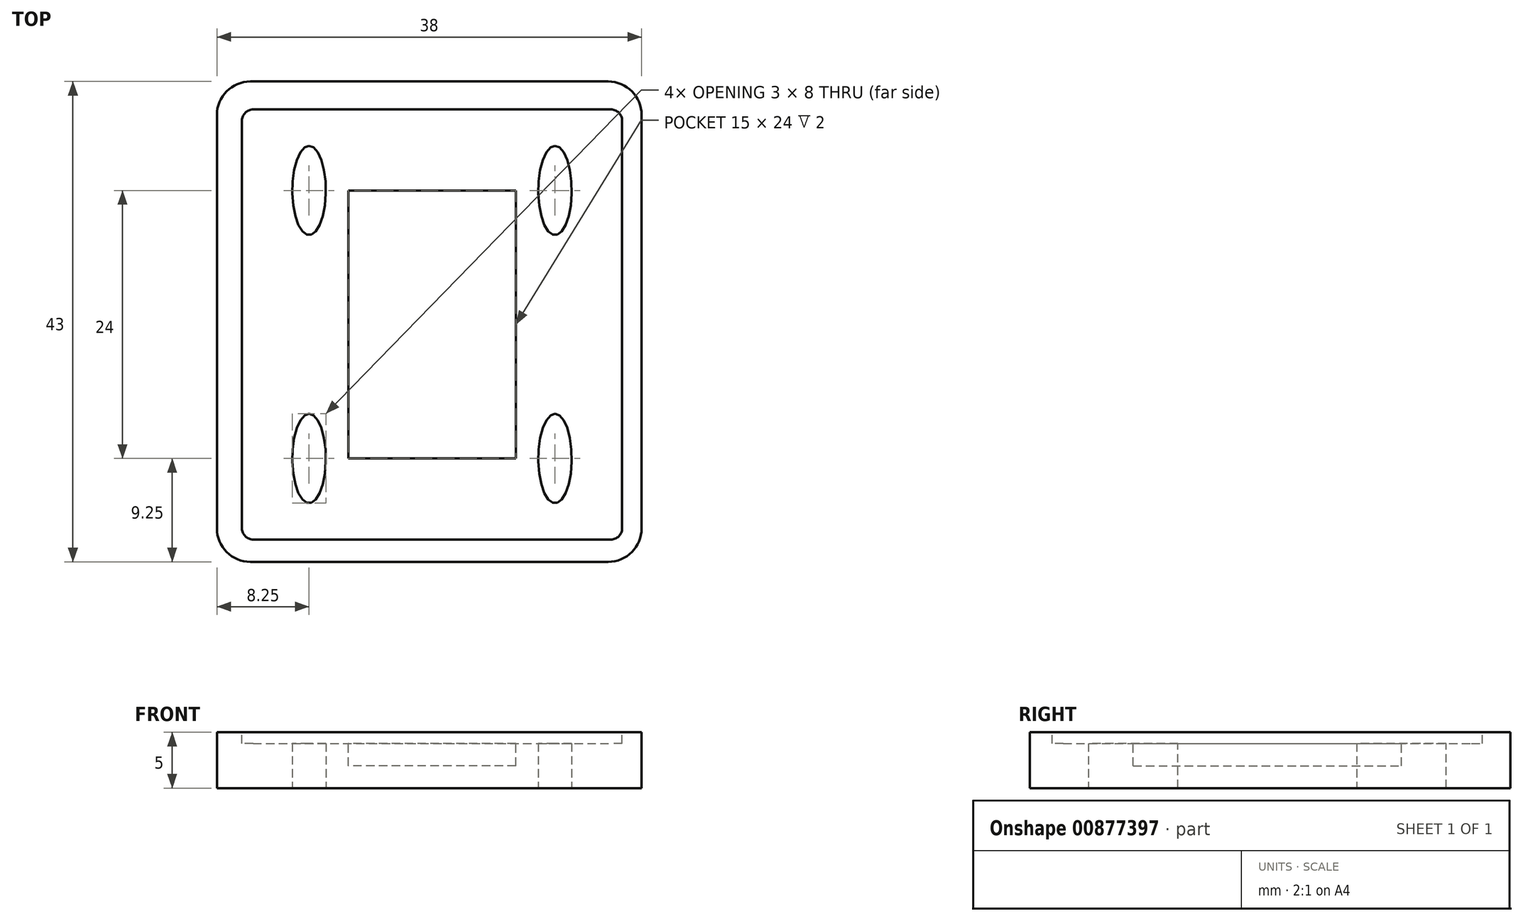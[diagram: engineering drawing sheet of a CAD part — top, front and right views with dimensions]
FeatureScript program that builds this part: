
annotation { "Feature Type Name" : "Feature", "Feature Type Description" : "" }
export const myFeature = defineFeature(function(context is Context, id is Id, definition is map)
    precondition{}
    {
        {
            var Q0;
            Q0=qCreatedBy(makeId("Top.planeOp"),FACE);
            var sketch = newSketch(context, id + "F0", { "sketchPlane" : qUnion([Q0])});
            skLineSegment(sketch, "E0.bottom", {"start": v(0, 0) * mm, "end": v(38, 0) * mm});
            skLineSegment(sketch, "E0.top", {"start": v(0, 43) * mm, "end": v(38, 43) * mm});
            skLineSegment(sketch, "E0.left", {"start": v(0, 0) * mm, "end": v(0, 43) * mm});
            skLineSegment(sketch, "E0.right", {"start": v(38, 0) * mm, "end": v(38, 43) * mm});
            skSolve(sketch);
        }
        {
            var Q0;
            Q0 = qSketchRegion(id + "F0", true);
            var Q1;
            Q1=makeQuery(id+"F0.imprint","IMPRINT",FACE,{"disambiguationData":[TD([[makeQuery(id+"F0.imprint","IMPRINT",EDGE,{"derivedFrom":sQuery(id+"F0.wireOp",EDGE,"M4hEIno1-cevh-JGJ9-cI0y-gHAv0wphkMzr")}),1.0]])]});
            extrude(context, id + "F1", {"entities" : qUnion([Q0, Q1]), "depth" : 5 * mm, "offsetDistance" : 25 * mm});
        }
        {
            var Q0;
            Q0=makeQuery(id+"F1.opExtrude","CAP_FACE",FACE,{"disambiguationData":[OSD([sQuery(id+"F0.wireOp",EDGE,"E0.bottom"),sQuery(id+"F0.wireOp",EDGE,"E0.top"),sQuery(id+"F0.wireOp",EDGE,"E0.left"),sQuery(id+"F0.wireOp",EDGE,"E0.right")])],"isStart":false});
            var sketch = newSketch(context, id + "F2", { "sketchPlane" : qUnion([Q0])});
            skLineSegment(sketch, "E1.bottom", {"start": v(2.25, 2) * mm, "end": v(36.25, 2) * mm});
            skLineSegment(sketch, "E1.top", {"start": v(2.25, 40.5) * mm, "end": v(36.25, 40.5) * mm});
            skLineSegment(sketch, "E1.left", {"start": v(2.25, 2) * mm, "end": v(2.25, 40.5) * mm});
            skLineSegment(sketch, "E1.right", {"start": v(36.25, 2) * mm, "end": v(36.25, 40.5) * mm});
            skSolve(sketch);
        }
        {
            var Q0;
            Q0=makeQuery(id+"F2.imprint","IMPRINT",FACE,{"disambiguationData":[TD([[makeQuery(id+"F2.imprint","IMPRINT",EDGE,{"derivedFrom":sQuery(id+"F2.wireOp",EDGE,"E1.bottom")}),1.0]])]});
            extrude(context, id + "F3", {"entities" : qUnion([Q0]), "operationType" : NewBodyOperationType.REMOVE, "oppositeDirection" : true, "depth" : 1 * mm, "offsetDistance" : 25 * mm});
        }
        {
            var Q0;
            Q0=makeQuery(id+"F3.boolean.opBoolean","COPY",FACE,{"derivedFrom":makeQuery(id+"F3.opExtrude","CAP_FACE",FACE,{"disambiguationData":[OSD([sQuery(id+"F2.wireOp",EDGE,"E1.bottom"),sQuery(id+"F2.wireOp",EDGE,"E1.top"),sQuery(id+"F2.wireOp",EDGE,"E1.left"),sQuery(id+"F2.wireOp",EDGE,"E1.right")])],"isStart":false})});
            var sketch = newSketch(context, id + "F4", { "sketchPlane" : qUnion([Q0])});
            skEllipse(sketch, "E2", {"center": v(8.25, 9.25) * mm, "majorRadius": 4 * mm, "minorRadius": 1.5 * mm, "majorAxis": v(0, 1)});
            skEllipse(sketch, "E3.0.1.0", {"center": v(8.25, 33.25) * mm, "majorRadius": 4 * mm, "minorRadius": 1.5 * mm, "majorAxis": v(0, 1)});
            skEllipse(sketch, "E3.1.0.0", {"center": v(30.25, 9.25) * mm, "majorRadius": 4 * mm, "minorRadius": 1.5 * mm, "majorAxis": v(0, 1)});
            skEllipse(sketch, "E3.1.1.0", {"center": v(30.25, 33.25) * mm, "majorRadius": 4 * mm, "minorRadius": 1.5 * mm, "majorAxis": v(0, 1)});
            skLineSegment(sketch, "E3.direction2", {"start": v(8.25, 9.25) * mm, "end": v(8.25, 33.25) * mm, "construction": true});
            skLineSegment(sketch, "E4.bottom", {"start": v(26.75, 9.25) * mm, "end": v(11.75, 9.25) * mm});
            skLineSegment(sketch, "E4.top", {"start": v(26.75, 33.25) * mm, "end": v(11.75, 33.25) * mm});
            skLineSegment(sketch, "E4.left", {"start": v(26.75, 9.25) * mm, "end": v(26.75, 33.25) * mm});
            skLineSegment(sketch, "E4.right", {"start": v(11.75, 9.25) * mm, "end": v(11.75, 33.25) * mm});
            skSolve(sketch);
        }
        {
            var Q0;
            Q0=makeQuery(id+"F4.imprint","IMPRINT",FACE,{"disambiguationData":[TD([[makeQuery(id+"F4.imprint","IMPRINT",EDGE,{"derivedFrom":sQuery(id+"F4.wireOp",EDGE,"E3.0.1.0")}),1.0]])]});
            var Q1;
            Q1=makeQuery(id+"F4.imprint","IMPRINT",FACE,{"disambiguationData":[TD([[makeQuery(id+"F4.imprint","IMPRINT",EDGE,{"derivedFrom":sQuery(id+"F4.wireOp",EDGE,"E3.1.1.0")}),1.0]])]});
            var Q2;
            Q2=makeQuery(id+"F4.imprint","IMPRINT",FACE,{"disambiguationData":[TD([[makeQuery(id+"F4.imprint","IMPRINT",EDGE,{"derivedFrom":sQuery(id+"F4.wireOp",EDGE,"E3.1.0.0")}),1.0]])]});
            var Q3;
            Q3=makeQuery(id+"F4.imprint","IMPRINT",FACE,{"disambiguationData":[TD([[makeQuery(id+"F4.imprint","IMPRINT",EDGE,{"derivedFrom":sQuery(id+"F4.wireOp",EDGE,"E2")}),1.0]])]});
            extrude(context, id + "F5", {"entities" : qUnion([Q0, Q1, Q2, Q3]), "operationType" : NewBodyOperationType.REMOVE, "oppositeDirection" : true, "depth" : 25 * mm, "offsetDistance" : 25 * mm});
        }
        {
            var Q0;
            Q0=makeQuery(id+"F1.opExtrude","SWEPT_EDGE",EDGE,{"disambiguationData":[OSD([sQuery(id+"F0.wireOp",EDGE,"E0.bottom"),sQuery(id+"F0.wireOp",EDGE,"E0.left")])]});
            var Q1;
            Q1=makeQuery(id+"F1.opExtrude","SWEPT_EDGE",EDGE,{"disambiguationData":[OSD([sQuery(id+"F0.wireOp",EDGE,"E0.bottom"),sQuery(id+"F0.wireOp",EDGE,"E0.right")])]});
            var Q2;
            Q2=makeQuery(id+"F1.opExtrude","SWEPT_EDGE",EDGE,{"disambiguationData":[OSD([sQuery(id+"F0.wireOp",EDGE,"E0.top"),sQuery(id+"F0.wireOp",EDGE,"E0.left")])]});
            var Q3;
            Q3=makeQuery(id+"F1.opExtrude","SWEPT_EDGE",EDGE,{"disambiguationData":[OSD([sQuery(id+"F0.wireOp",EDGE,"E0.top"),sQuery(id+"F0.wireOp",EDGE,"E0.right")])]});
            fillet(context, id + "F6", {"entities" : qUnion([Q0, Q1, Q2, Q3]), "radius" : 3 * mm, "tangentPropagation" : true, "allowEdgeOverflow" : false});
        }
        {
            var Q0;
            Q0=makeQuery(id+"F3.boolean.opBoolean","COPY",EDGE,{"derivedFrom":makeQuery(id+"F3.opExtrude","SWEPT_EDGE",EDGE,{"disambiguationData":[OSD([sQuery(id+"F2.wireOp",EDGE,"E1.bottom"),sQuery(id+"F2.wireOp",EDGE,"E1.left")])]})});
            var Q1;
            Q1=makeQuery(id+"F3.boolean.opBoolean","COPY",EDGE,{"derivedFrom":makeQuery(id+"F3.opExtrude","SWEPT_EDGE",EDGE,{"disambiguationData":[OSD([sQuery(id+"F2.wireOp",EDGE,"E1.top"),sQuery(id+"F2.wireOp",EDGE,"E1.left")])]})});
            var Q2;
            Q2=makeQuery(id+"F3.boolean.opBoolean","COPY",EDGE,{"derivedFrom":makeQuery(id+"F3.opExtrude","SWEPT_EDGE",EDGE,{"disambiguationData":[OSD([sQuery(id+"F2.wireOp",EDGE,"E1.bottom"),sQuery(id+"F2.wireOp",EDGE,"E1.right")])]})});
            var Q3;
            Q3=makeQuery(id+"F3.boolean.opBoolean","COPY",EDGE,{"derivedFrom":makeQuery(id+"F3.opExtrude","SWEPT_EDGE",EDGE,{"disambiguationData":[OSD([sQuery(id+"F2.wireOp",EDGE,"E1.top"),sQuery(id+"F2.wireOp",EDGE,"E1.right")])]})});
            fillet(context, id + "F7", {"entities" : qUnion([Q0, Q1, Q2, Q3]), "radius" : 1 * mm, "tangentPropagation" : true, "allowEdgeOverflow" : false});
        }
        {
            var Q0;
            Q0=makeQuery(id+"F4.imprint","IMPRINT",FACE,{"disambiguationData":[TD([[makeQuery(id+"F4.imprint","IMPRINT",EDGE,{"derivedFrom":sQuery(id+"F4.wireOp",EDGE,"E4.bottom")}),-1.0]])]});
            extrude(context, id + "F8", {"entities" : qUnion([Q0]), "operationType" : NewBodyOperationType.REMOVE, "oppositeDirection" : true, "depth" : 2 * mm, "offsetDistance" : 25 * mm});
        }
    });
